# Revit family: Refrigerador
name_source: partatom
category: Modelos genéricos
units: mm (PartAtom-declared; Revit-internal decimal feet)

## family parameters
Compartilhado = Sim
Corte com vazios quando carregada = Não
Cota do conector redondo = Utilizar diâmetro
Pode hospedar o vergalhão = Não
Ponto de cálculo do ambiente = Não
Sempre na vertical = Não
Tipo de parte = Não definido

## types (1)
- Refrigerador
    Alerta de porta aberta = Sim
    Capacidade total (litros) = 250 L
    Capacidade útil (litros) = Refrigerador: 167 L. Freezer: 64 L
    Desligamento do compartimento do refrigerador = Sim
    Elevação padrão = 0 mm  [stored 0 ft]
    Fabricante = Tramontina
    Freezer com ajuste de temperatua = 02 ºC à 08 ºC
    Frequência = -12 ºC à -24 ºC
    Função congelamento rápido = Sim
    Função férias = Sim, para uso reduzido do refrigerador, essa função economiza energia
    Função resfriamento rápido = Sim
    Iluminação = 2 W
    Instalação = Embutir
    Kit de instalação = Sim
    Modelo = Refrigerador de embutir
    Painel de comando = Touch
    Potência Elétrica (W) = 265 W
    Referência = 94897/001
    Refrigerador com ajuste de temperatura = 02 ºC a 08 ºC
    Tensão = 220 V
    URL = www.tramontina.com.br

note: [stored X ft] marks values corroborated as IEEE doubles in the binary element streams (Revit-internal decimal feet)
